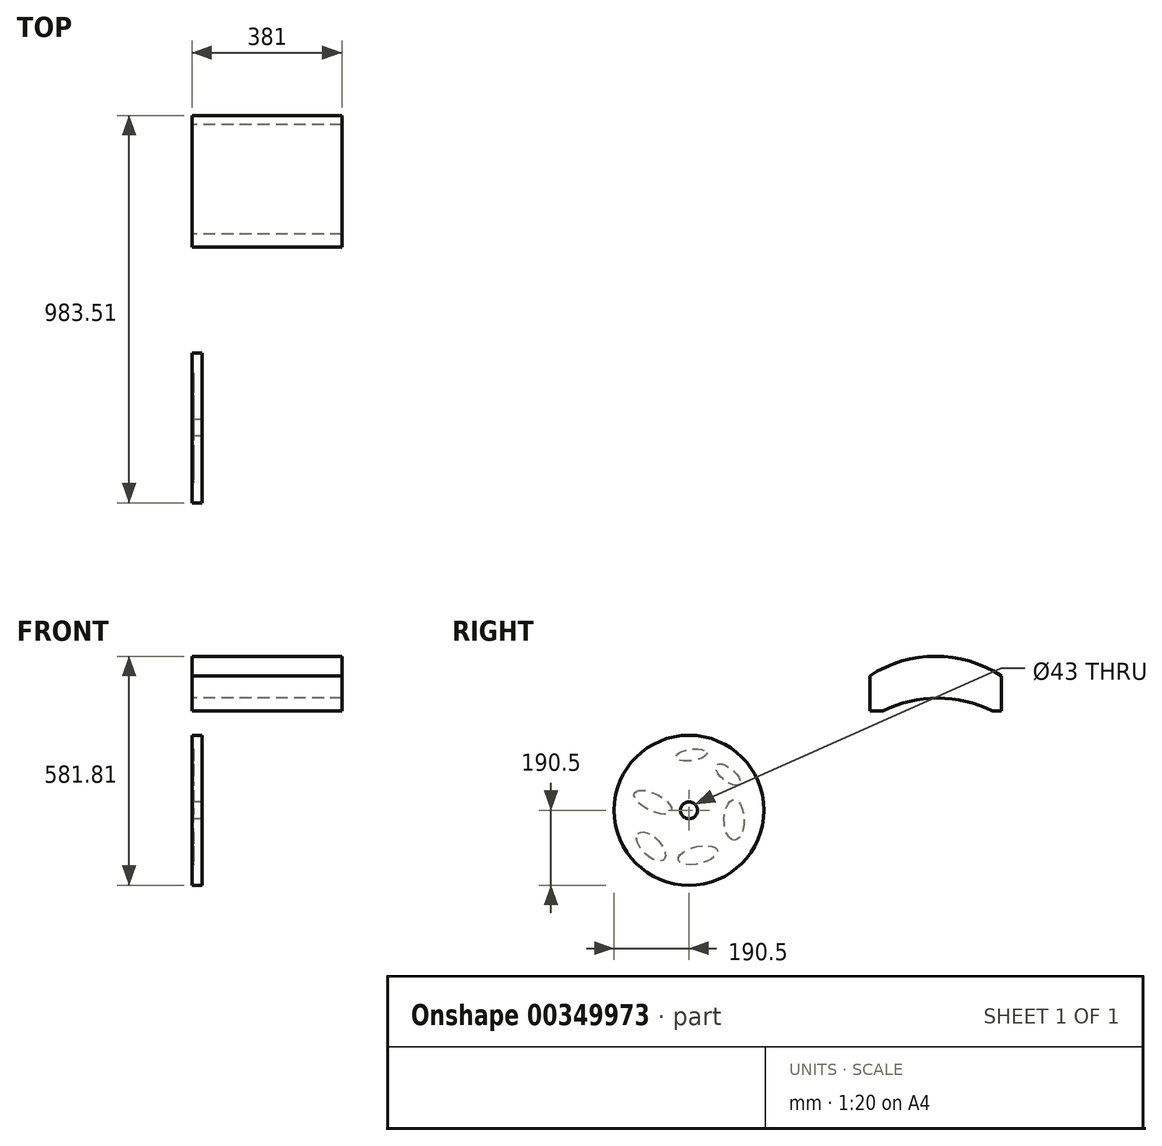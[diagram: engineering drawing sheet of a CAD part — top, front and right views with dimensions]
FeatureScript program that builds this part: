
annotation { "Feature Type Name" : "Feature", "Feature Type Description" : "" }
export const myFeature = defineFeature(function(context is Context, id is Id, definition is map)
    precondition{}
    {
        {
            var Q0;
            Q0=qCreatedBy(makeId("Right.planeOp"),FACE);
            var sketch = newSketch(context, id + "F0", { "sketchPlane" : qUnion([Q0])});
            skCircle(sketch, "E0", {"center": v(0, 0) * mm, "radius": 190.5 * mm});
            skSolve(sketch);
        }
        {
            var Q0;
            Q0 = qSketchRegion(id + "F0", true);
            extrude(context, id + "F1", {"entities" : qUnion([Q0]), "depth" : 25.4 * mm});
        }
        {
            var Q0;
            Q0=makeQuery(id+"F1.opExtrude","CAP_FACE",FACE,{"disambiguationData":[OSD([sQuery(id+"F0.wireOp",EDGE,"E0")])],"isStart":true});
            var sketch = newSketch(context, id + "F2", { "sketchPlane" : qUnion([Q0])});
            skCircle(sketch, "E1", {"center": v(0, 0) * mm, "radius": 21.5 * mm});
            skSolve(sketch);
        }
        {
            var Q0;
            Q0 = qSketchRegion(id + "F2", true);
            extrude(context, id + "F3", {"entities" : qUnion([Q0]), "operationType" : NewBodyOperationType.REMOVE, "oppositeDirection" : true, "depth" : 72.64 * mm});
        }
        {
            var Q0;
            Q0=makeQuery(id+"F1.opExtrude","CAP_FACE",FACE,{"disambiguationData":[OSD([sQuery(id+"F0.wireOp",EDGE,"E0")])],"isStart":true});
            var sketch = newSketch(context, id + "F4", { "sketchPlane" : qUnion([Q0])});
            skEllipse(sketch, "E2", {"center": v(-6.37, 140.51) * mm, "majorRadius": 39.36 * mm, "minorRadius": 14.6 * mm, "majorAxis": v(-1, 0.14)});
            skEllipse(sketch, "E3", {"center": v(-99.02, 90.37) * mm, "majorRadius": 37.99 * mm, "minorRadius": 16.6 * mm, "majorAxis": v(-0.77, -0.64)});
            skEllipse(sketch, "E4", {"center": v(-114.37, -25.07) * mm, "majorRadius": 51.38 * mm, "minorRadius": 25.34 * mm, "majorAxis": v(0, -1)});
            skEllipse(sketch, "E5", {"center": v(-22.44, -114.1) * mm, "majorRadius": 51.24 * mm, "minorRadius": 21.56 * mm, "majorAxis": v(0.97, -0.24)});
            skEllipse(sketch, "E6", {"center": v(96.5, -92.26) * mm, "majorRadius": 46.54 * mm, "minorRadius": 23.33 * mm, "majorAxis": v(0.7, 0.71)});
            skEllipse(sketch, "E7", {"center": v(91.78, 20.56) * mm, "majorRadius": 52.1 * mm, "minorRadius": 22.17 * mm, "majorAxis": v(0.9, 0.44)});
            skSolve(sketch);
        }
        {
            var Q0;
            Q0 = qSketchRegion(id + "F4", true);
            extrude(context, id + "F5", {"entities" : qUnion([Q0]), "operationType" : NewBodyOperationType.REMOVE, "oppositeDirection" : true, "depth" : 3.8 * mm});
        }
        {
            var Q0;
            Q0=qCreatedBy(makeId("Right.planeOp"),FACE);
            var sketch = newSketch(context, id + "F6", { "sketchPlane" : qUnion([Q0])});
            skLineSegment(sketch, "E8", {"start": v(459.32, 341.85) * mm, "end": v(459.32, 251.85) * mm});
            skLineSegment(sketch, "E9", {"start": v(459.32, 251.85) * mm, "end": v(492.69, 251.85) * mm});
            skArc(sketch, "E10", {"start": v(793, 341.85) * mm, "mid": v(626.16, 391.31) * mm, "end": v(459.32, 341.85) * mm});
            skLineSegment(sketch, "E11", {"start": v(793, 341.85) * mm, "end": v(793, 251.85) * mm});
            skPoint(sketch, "E11.endSnap0", {"position": v(476, 251.85) * mm});
            skLineSegment(sketch, "E12", {"start": v(793, 251.85) * mm, "end": v(770.76, 251.85) * mm});
            skArc(sketch, "E13", {"start": v(770.76, 251.85) * mm, "mid": v(631.73, 285.22) * mm, "end": v(492.69, 251.85) * mm});
            skSolve(sketch);
        }
        {
            var Q0;
            Q0 = qSketchRegion(id + "F6", true);
            extrude(context, id + "F7", {"entities" : qUnion([Q0]), "depth" : 381 * mm, "offsetDistance" : 25.4 * mm});
        }
    });
